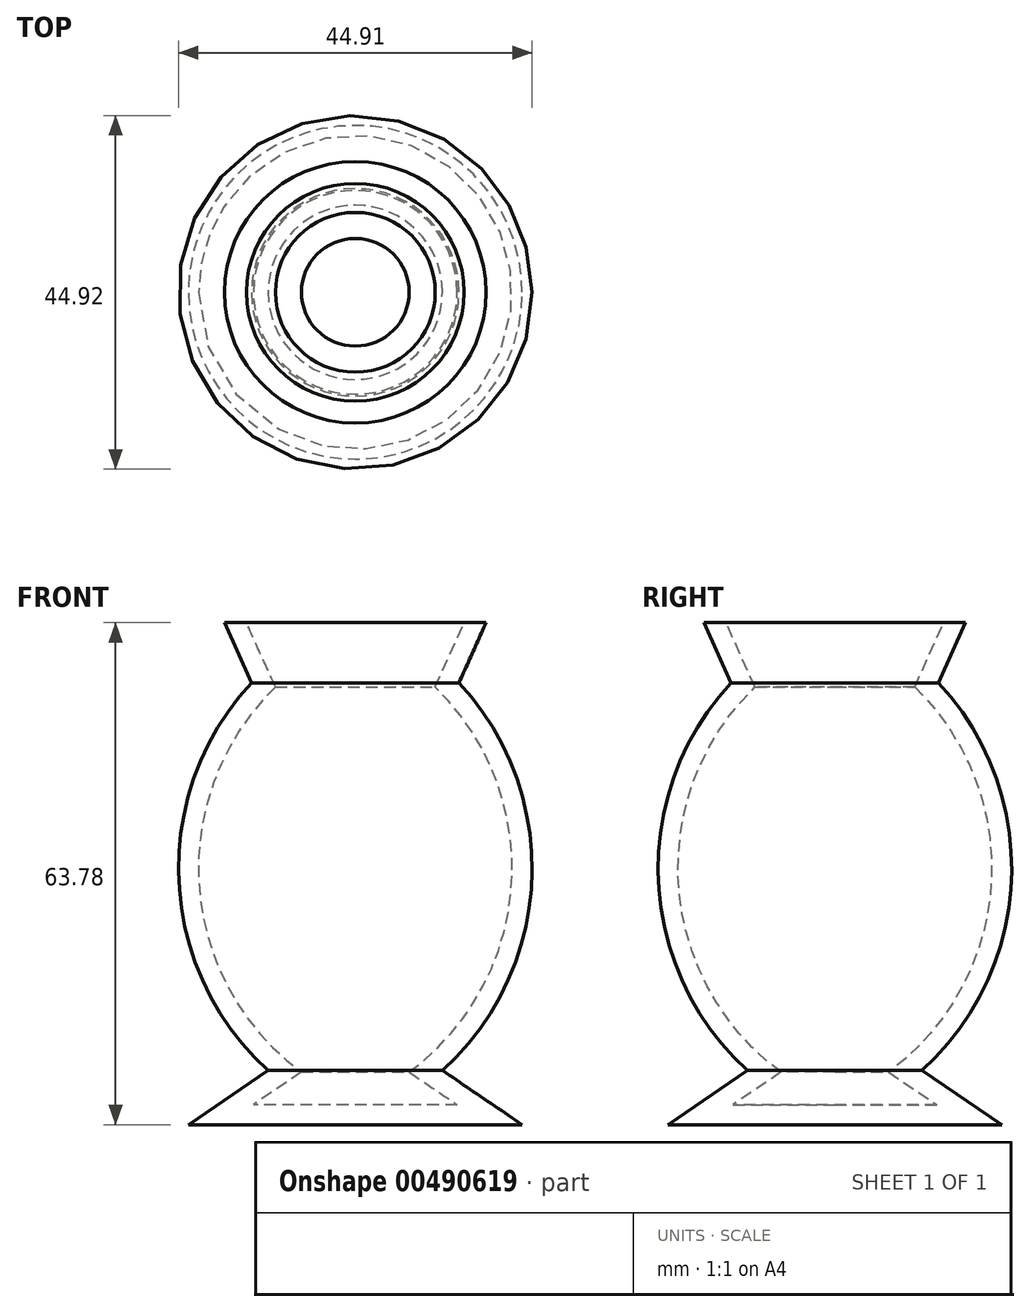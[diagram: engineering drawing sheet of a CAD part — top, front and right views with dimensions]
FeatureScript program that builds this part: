
annotation { "Feature Type Name" : "Feature", "Feature Type Description" : "" }
export const myFeature = defineFeature(function(context is Context, id is Id, definition is map)
    precondition{}
    {
        {
            var Q0;
            Q0=qCreatedBy(makeId("Front.planeOp"),FACE);
            var sketch = newSketch(context, id + "F0", { "sketchPlane" : qUnion([Q0])});
            skArc(sketch, "E0", {"start": v(-32.46, 27.88) * mm, "mid": v(-41.71, 2.8) * mm, "end": v(-30.36, -21.39) * mm});
            skLineSegment(sketch, "E1", {"start": v(-32.46, 27.88) * mm, "end": v(-35.9, 35.52) * mm});
            skLineSegment(sketch, "E2", {"start": v(-35.9, 35.52) * mm, "end": v(-19.29, 35.52) * mm});
            skLineSegment(sketch, "E3", {"start": v(-19.29, 35.52) * mm, "end": v(-19.29, -28.26) * mm});
            skLineSegment(sketch, "E4", {"start": v(-19.29, -28.26) * mm, "end": v(-40.48, -28.26) * mm});
            skLineSegment(sketch, "E5", {"start": v(-40.48, -28.26) * mm, "end": v(-30.36, -21.39) * mm});
            skLineSegment(sketch, "E6", {"start": v(-32.46, 27.88) * mm, "end": v(-36.66, 32.65) * mm});
            skLineSegment(sketch, "E7", {"start": v(-36.66, 32.65) * mm, "end": v(-40.86, 35.33) * mm});
            skLineSegment(sketch, "E8", {"start": v(-40.86, 35.33) * mm, "end": v(-45.83, 35.33) * mm});
            skArc(sketch, "E9", {"start": v(-45.83, 35.33) * mm, "mid": v(-53.5, 15.53) * mm, "end": v(-41.21, -1.78) * mm});
            skArc(sketch, "E10.MirrorCS", {"start": v(7.26, 35.33) * mm, "mid": v(14.92, 15.53) * mm, "end": v(2.64, -1.78) * mm});
            skLineSegment(sketch, "E11.MirrorCS", {"start": v(2.3, 35.33) * mm, "end": v(7.26, 35.33) * mm});
            skLineSegment(sketch, "E12.MirrorCS", {"start": v(-1.9, 32.65) * mm, "end": v(2.3, 35.33) * mm});
            skLineSegment(sketch, "E13.MirrorCS", {"start": v(-6.11, 27.88) * mm, "end": v(-1.9, 32.65) * mm});
            skSolve(sketch);
        }
        {
            var Q0;
            {var subQ0=sQuery(id+"F0.wireOp",EDGE,"E1");Q0=makeQuery(id+"F0.imprint","IMPRINT",FACE,{"disambiguationData":[TD([[makeQuery(id+"F0.imprint","IMPRINT",EDGE,{"derivedFrom":subQ0}),-1.0]])]});}
            var Q1;
            Q1=sQuery(id+"F0.wireOp",EDGE,"E3");
            revolve(context, id + "F1", {"entities" : qUnion([Q0]), "axis" : qUnion([Q1]), "revolveType" : RevolveType.FULL});
        }
        {
            var Q0;
            Q0=makeQuery(id+"F1.opRevolve","SWEPT_FACE",FACE,{"disambiguationData":[OSD([sQuery(id+"F0.wireOp",EDGE,"E2")])]});
            shell(context, id + "F2", {"entities" : qUnion([Q0]), "thickness" : 2.54 * mm});
        }
        {
            var Q0;
            Q0=sQuery(id+"F0.wireOp",EDGE,"E6");
            var Q1;
            Q1=sQuery(id+"F0.wireOp",EDGE,"E7");
            var Q2;
            Q2=sQuery(id+"F0.wireOp",EDGE,"E8");
            var Q3;
            Q3=sQuery(id+"F0.wireOp",EDGE,"E9");
            extrude(context, id + "F3", {"bodyType" : ToolBodyType.SURFACE, "surfaceEntities" : qUnion([Q0, Q1, Q2, Q3]), "endBound" : BoundingType.SYMMETRIC, "depth" : 10.16 * mm});
        }
        {
            var Q0;
            Q0=sQuery(id+"F0.wireOp",EDGE,"E10.MirrorCS");
            var Q1;
            Q1=sQuery(id+"F0.wireOp",EDGE,"E11.MirrorCS");
            var Q2;
            Q2=sQuery(id+"F0.wireOp",EDGE,"E12.MirrorCS");
            var Q3;
            Q3=sQuery(id+"F0.wireOp",EDGE,"E13.MirrorCS");
            extrude(context, id + "F4", {"bodyType" : ToolBodyType.SURFACE, "surfaceEntities" : qUnion([Q0, Q1, Q2, Q3]), "endBound" : BoundingType.SYMMETRIC, "depth" : 10.16 * mm});
        }
    });
